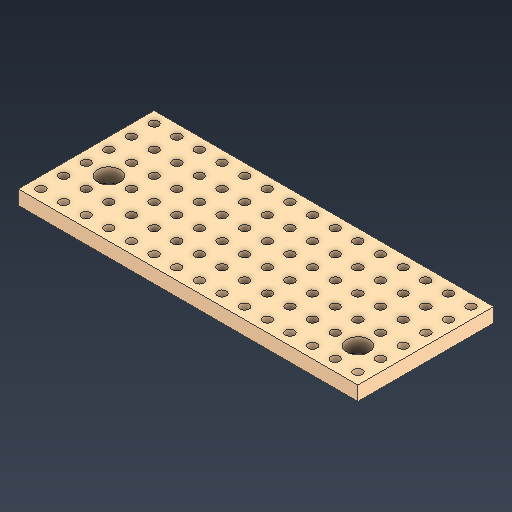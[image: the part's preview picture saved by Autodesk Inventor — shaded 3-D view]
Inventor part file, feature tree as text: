
AUTODESK INVENTOR PART (.ipt)
format: ipt  version: 2021 (Build 250183000, 183)  size: 313,344 bytes
history: native  units: mm
features: extrude x2, sketch x2
ambient origin geometry x8: Origin, YZ Plane, XZ Plane, XY Plane, X Axis, Y Axis, Z Axis, Center Point
bodies: Solid1 (feature_tree)
feature tree (4):
  extrude  "Extrusion1"  Depth=15.24mm
  extrude  "Extrusion2"  Depth=1.6mm
  sketch  "Sketch1"  dims[d0=38.1mm d1=15.24mm]
  sketch  "Sketch3"  dims[d2=1.0mm d3=150.0mm d5=2.54mm d6=60.0mm d8=2.54mm d11=1.27mm d12=1.27mm d13=1.6mm d14=0.0mm d15=2.5mm d16=2.5mm d17=3.81mm d18=3.81mm d19=8.89mm d20=11.43mm d21=1.6mm d22=0.0mm]
